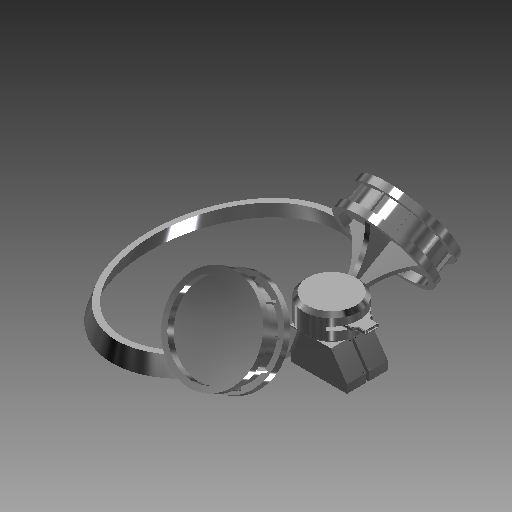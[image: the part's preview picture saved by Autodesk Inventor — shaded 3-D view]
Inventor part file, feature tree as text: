
AUTODESK INVENTOR PART (.ipt)
format: ipt  version: 2021 (Build 250183000, 183)  size: 799,232 bytes
history: native  units: in
note: dims shown in document units (in); Inventor stores cm internally (conversion verified against a paired STEP export)
features: extrude x21, sketch x19, plane x10, mirror x5, fillet x3, loft x2, chamfer x1, other x1, pattern_circular x1
ambient origin geometry x8: Origin, YZ Plane, XZ Plane, XY Plane, X Axis, Y Axis, Z Axis, Center Point
bodies: Solid1 (feature_tree)
feature tree (63):
  extrude  "Extrusion1"  Depth=1.15in
  extrude  "Extrusion2"  Depth=2.0in TaperAngle=0.0deg
  extrude  "Extrusion3"  Depth=0.05in TaperAngle=0.0deg
  extrude  "Extrusion4"  Depth=0.4in
  chamfer  "Chamfer1"  Distance=0.65in
  extrude  "Extrusion5"  Depth=0.01in TaperAngle=0.0deg
  extrude  "Extrusion6"  Depth=1.0in TaperAngle=0.0deg
  extrude  "Extrusion7"  Depth=0.1in TaperAngle=0.0deg
  plane  "Work Plane1"
  extrude  "Extrusion8"  Depth=0.06in
  extrude  "Extrusion9"  Depth=0.026in
  extrude  "Extrusion10"  Depth=0.8in TaperAngle=0.0deg
  extrude  "Extrusion11"  TaperAngle=60.0deg  [1 undecoded]
  fillet  "Fillet1"  Radius=0.075in
  fillet  "Fillet2"  Radius=0.1in
  fillet  "Fillet3"  Radius=1.441in
  extrude  "Extrusion12"  Depth=0.1092in
  extrude  "Extrusion13"  Depth=0.72in
  extrude  "Extrusion14"  Depth=0.1in TaperAngle=0.0deg
  plane  "Work Plane2"
  extrude  "Extrusion15"  Depth=0.15in TaperAngle=0.0deg
  plane  "Work Plane3"
  mirror  "Mirror1"
  plane  "Work Plane4"
  extrude  "Extrusion16"  [1 undecoded]
  plane  "Work Plane5"
  mirror  "Mirror2"
  plane  "Work Plane6"
  sketch  "Sketch17"  dims[d29=0.2in d30=0.0in d31=0.06in]
  extrude  "Extrusion17"  Depth=0.5in TaperAngle=0.0deg
  mirror  "Mirror3"
  extrude  "Extrusion18"  [1 undecoded]
  extrude  "Extrusion19"  TaperAngle=0.0deg  [1 undecoded]
  extrude  "Extrusion20"  TaperAngle=0.0deg  [1 undecoded]
  mirror  "Mirror4"
  plane  "Work Plane7"
  extrude  "Extrusion22"  TaperAngle=0.0deg  [1 undecoded]
  other  "Work Axis1"
  pattern_circular  "Circular Pattern1"  Angle=90.0deg  [1 undecoded]
  plane  "Work Plane8"
  mirror  "Mirror5"
  sketch  "Sketch25"  dims[d51=0.109in d52=0.1in d53=0.0in]
  sketch  "Sketch26"  dims[d54=0.35in d55=0.0in d56=0.15in d57=0.0in]
  plane  "Work Plane9"
  plane  "Work Plane10"
  loft  "Loft1"
  loft  "Loft2"
  sketch  "Sketch1"  dims[d0=0.85in d1=1.15in]
  sketch  "Sketch8"  dims[d2=0.65in d3=0.0in d4=2.0in d5=0.0in]
  sketch  "Sketch10"  dims[d6=0.6in d7=0.0in d8=0.05in d9=0.0in]
  sketch  "Sketch12"  dims[d10=0.075in d11=0.125in d12=45.0deg d13=0.4in]
  sketch  "Sketch13"  dims[d14=0.4in d15=0.65in d16=0.0in]
  sketch  "Sketch14"  dims[d18=0.1in d19=0.0in d20=0.01in d21=0.0in]
  sketch  "Sketch15"  dims[d22=0.0in d23=1.0in d24=0.0in]
  sketch  "Sketch16"  dims[d25=1.0in d26=0.0in d27=0.1in d28=0.0in]
  sketch  "Sketch18"  dims[d32=0.03in d33=0.026in]
  sketch  "Sketch19"  dims[d34=0.8in d35=0.0in d36=0.8in d37=0.0in]
  sketch  "Sketch21"  dims[d38=0.8in d39=0.0in d40=60.0deg d41=0.075in d42=0.0in d43=0.1in d44=0.0in d45=1.441in]
  sketch  "Sketch22"  dims[d46=1.208in d47=0.1092in]
  sketch  "Sketch24"  dims[d48=1.0606in d50=0.72in]
  sketch  "Sketch28"  dims[d58=0.15in d59=0.0in d60=-0.05in]
  sketch  "Sketch29"  dims[d63=4.7244in d65=360.0deg d67=0.5in d68=0.0in]
  sketch  "Sketch30"  dims[d69=3.937in d70=360.0deg d72=-0.25in d73=-0.35in d74=0.0in d75=90.0deg d76=0.0in d77=90.0deg d78=0.0in d79=90.0deg d80=0.0in d81=90.0deg]
note: 7 required parameter values undecoded (feature->parameter linkage not recoverable at this tier; creation-order binding heuristic only, values carry confidence <= 0.55)
